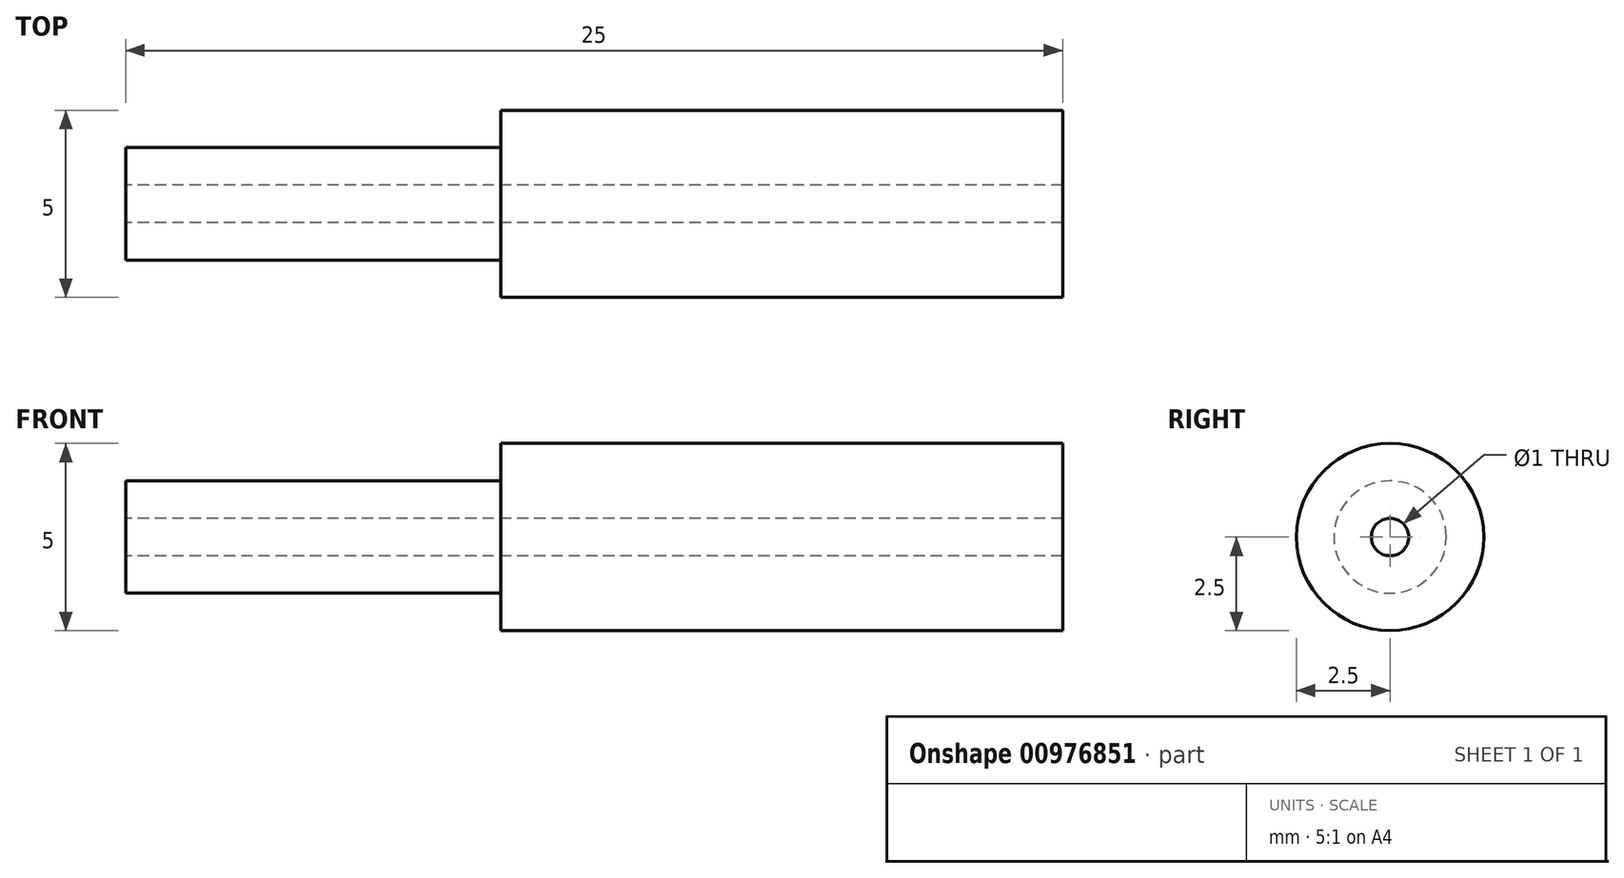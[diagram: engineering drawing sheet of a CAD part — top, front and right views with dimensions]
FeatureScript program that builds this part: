
annotation { "Feature Type Name" : "Feature", "Feature Type Description" : "" }
export const myFeature = defineFeature(function(context is Context, id is Id, definition is map)
    precondition{}
    {
        {
            var Q0;
            Q0=qCreatedBy(makeId("Front.planeOp"),FACE);
            var sketch = newSketch(context, id + "F0", { "sketchPlane" : qUnion([Q0])});
            skLineSegment(sketch, "E0.top", {"start": v(0, 0.5) * mm, "end": v(25, 0.5) * mm});
            skLineSegment(sketch, "E0.left", {"start": v(0, 1.5) * mm, "end": v(0, 0.5) * mm});
            skLineSegment(sketch, "E1", {"start": v(0, 1.5) * mm, "end": v(10, 1.5) * mm});
            skLineSegment(sketch, "E2", {"start": v(10, 1.5) * mm, "end": v(10, 2.5) * mm});
            skLineSegment(sketch, "E3", {"start": v(10, 2.5) * mm, "end": v(25, 2.5) * mm});
            skLineSegment(sketch, "E4", {"start": v(25, 2.5) * mm, "end": v(25, 0.5) * mm});
            skLineSegment(sketch, "E5", {"start": v(0, 0) * mm, "end": v(18.96, 0) * mm});
            skSolve(sketch);
        }
        {
            var Q0;
            Q0=makeQuery(id+"F0.imprint","IMPRINT",FACE,{"disambiguationData":[TD([[makeQuery(id+"F0.imprint","IMPRINT",EDGE,{"derivedFrom":sQuery(id+"F0.wireOp",EDGE,"E0.top")}),1.0]])]});
            var Q1;
            Q1=sQuery(id+"F0.wireOp",EDGE,"E5");
            revolve(context, id + "F1", {"surfaceOperationType" : NewSurfaceOperationType.NEW, "entities" : qUnion([Q0]), "axis" : qUnion([Q1]), "revolveType" : RevolveType.FULL});
        }
    });
